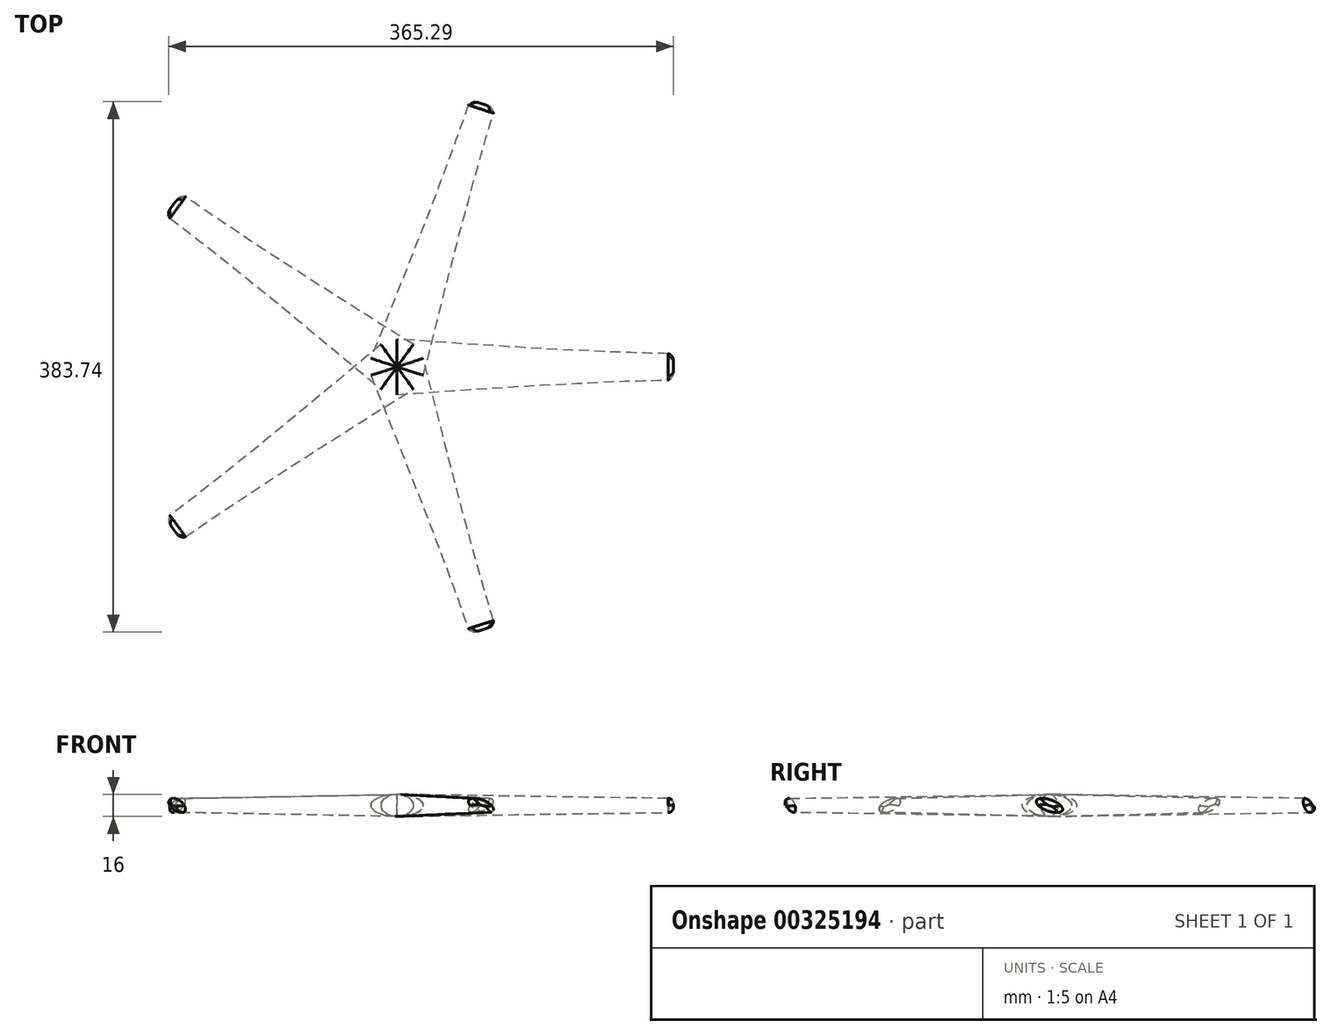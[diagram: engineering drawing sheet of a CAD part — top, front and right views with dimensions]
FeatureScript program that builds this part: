
annotation { "Feature Type Name" : "Feature", "Feature Type Description" : "" }
export const myFeature = defineFeature(function(context is Context, id is Id, definition is map)
    precondition{}
    {
        {
            var Q0;
            Q0=qCreatedBy(makeId("Right.planeOp"),FACE);
            var sketch = newSketch(context, id + "F0", { "sketchPlane" : qUnion([Q0])});
            skEllipse(sketch, "E0", {"center": v(0, 0) * mm, "majorRadius": 20 * mm, "minorRadius": 8 * mm, "majorAxis": v(1, 0)});
            skSolve(sketch);
        }
        {
            var Q0;
            Q0=qCreatedBy(makeId("Right.planeOp"),FACE);
            cPlane(context, id + "F1", {"entities" : qUnion([Q0]), "cplaneType" : CPlaneType.OFFSET, "offset" : 200 * mm, "width" : 150 * mm, "height" : 150 * mm});
        }
        {
            var Q0;
            Q0=qCreatedBy(id+"F1.planeOp",FACE);
            var sketch = newSketch(context, id + "F2", { "sketchPlane" : qUnion([Q0])});
            skLineSegment(sketch, "E1", {"start": v(0, 0) * mm, "end": v(9.4, -3.42) * mm, "construction": true});
            skEllipse(sketch, "E2", {"center": v(0, 0) * mm, "majorRadius": 10 * mm, "minorRadius": 4 * mm, "majorAxis": v(0.94, -0.34)});
            skSolve(sketch);
        }
        {
            var Q0;
            Q0=makeQuery(id+"F2.imprint","IMPRINT",FACE,{"disambiguationData":[TD([[makeQuery(id+"F2.imprint","IMPRINT",EDGE,{"derivedFrom":sQuery(id+"F2.wireOp",EDGE,"E2")}),1.0]])]});
            var Q1;
            Q1=makeQuery(id+"F0.imprint","IMPRINT",FACE,{"disambiguationData":[TD([[makeQuery(id+"F0.imprint","IMPRINT",EDGE,{"derivedFrom":sQuery(id+"F0.wireOp",EDGE,"E0")}),1.0]])]});
            loft(context, id + "F3", {"sheetProfilesArray" : [{ "sheetProfileEntities" : qUnion([Q0]) }, { "sheetProfileEntities" : qUnion([Q1]) }]});
        }
        {
            var Q0;
            Q0=makeQuery(id+"F3.opLoft","MID_CAP_EDGE",EDGE,{"disambiguationData":[OSD([sQuery(id+"F2.wireOp",EDGE,"E2")])],"capPos":0.0});
            fillet(context, id + "F4", {"entities" : qUnion([Q0]), "radius" : 4 * mm, "tangentPropagation" : true, "allowEdgeOverflow" : false});
        }
        {
            var Q0;
            Q0=qCreatedBy(makeId("Right.planeOp"),FACE);
            var sketch = newSketch(context, id + "F5", { "sketchPlane" : qUnion([Q0])});
            skLineSegment(sketch, "E3", {"start": v(0, 0) * mm, "end": v(0, 118.42) * mm, "construction": true});
            skLineSegment(sketch, "E4", {"start": v(0, 0) * mm, "end": v(0, -161.7) * mm, "construction": true});
            skSolve(sketch);
        }
        {
            var Q0;
            Q0=makeQuery(id+"F3.opLoft","SWEPT_BODY",BODY,{"disambiguationData":[OSD([makeQuery(id+"F0.imprint","IMPRINT",FACE,{"disambiguationData":[TD([[makeQuery(id+"F0.imprint","IMPRINT",EDGE,{"derivedFrom":sQuery(id+"F0.wireOp",EDGE,"E0")}),1.0]])]}),makeQuery(id+"F2.imprint","IMPRINT",FACE,{"disambiguationData":[TD([[makeQuery(id+"F2.imprint","IMPRINT",EDGE,{"derivedFrom":sQuery(id+"F2.wireOp",EDGE,"E2")}),1.0]])]})])]});
            var Q1;
            Q1=sQuery(id+"F5.wireOp",EDGE,"E3");
            circularPattern(context, id + "F6", {"entities" : qUnion([Q0]), "axis" : qUnion([Q1]), "angle" : 360 * degree, "instanceCount" : 5, "oppositeDirection" : true, "equalSpace" : true});
        }
    });
